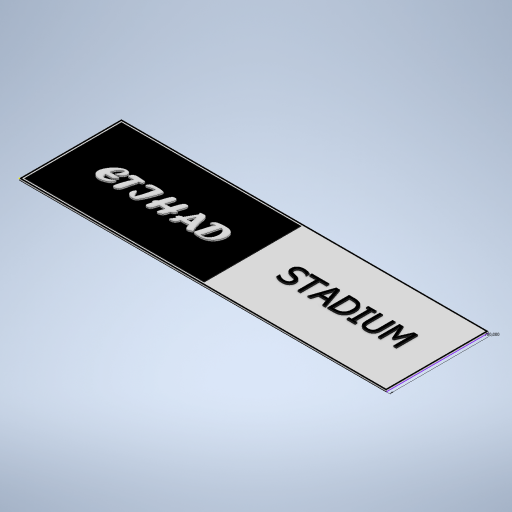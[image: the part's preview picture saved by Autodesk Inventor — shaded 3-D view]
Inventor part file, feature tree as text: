
AUTODESK INVENTOR PART (.ipt)
format: ipt  version: 2024.1 (Build 281209000, 209)  size: 1,069,568 bytes
history: native  units: in
note: dims shown in document units (in); Inventor stores cm internally (conversion verified against a paired STEP export)
features: extrude x7, sketch x3
ambient origin geometry x8: Origin, YZ Plane, XZ Plane, XY Plane, X Axis, Y Axis, Z Axis, Center Point
bodies: Solid1 (feature_tree), Solid3 (feature_tree)
feature tree (10):
  sketch  "Sketch1"  dims[d3=780.0in d4=10.0in]
  extrude  "Extrusion1"  Depth=10.0in
  extrude  "Extrusion2"  Depth=20.0in TaperAngle=0.0deg
  extrude  "Extrusion3"  Depth=10.0in TaperAngle=0.0deg
  extrude  "Extrusion4"  Depth=10.0in TaperAngle=0.0deg
  extrude  "Extrusion5"  Depth=11.0in TaperAngle=0.0deg
  sketch  "Sketch2"  dims[d7=20.0in d8=0.0in d9=20.0in d10=0.0in]
  extrude  "Extrusion7"  Depth=10.0in TaperAngle=0.0deg
  extrude  "Extrusion10"  Depth=10.0in
  sketch  "Sketch3"  dims[d11=10.0in d12=0.0in d13=10.0in d14=0.0in d15=10.0in d16=0.0in d19=11.0in d20=0.0in d39=10.0in d40=0.0in d17=0.5in d18=0.0344in d21=0.5in d22=0.0344in d36=0.5in d37=0.0344in d38=0.5in]
